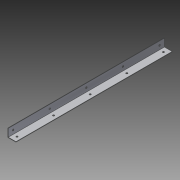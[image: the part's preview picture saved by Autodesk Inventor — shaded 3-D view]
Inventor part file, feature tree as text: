
AUTODESK INVENTOR PART (.ipt)
format: ipt  version: 2014 SP1 (Build 180222100, 222)  size: 107,520 bytes
history: native  units: in
note: dims shown in document units (in); Inventor stores cm internally (conversion verified against a paired STEP export)
features: extrude x3, sketch x3
ambient origin geometry x8: Origin, YZ Plane, XZ Plane, XY Plane, X Axis, Y Axis, Z Axis, Center Point
bodies: Solid1 (feature_tree)
feature tree (6):
  extrude  "Extrusion1"  Depth=0.0312in
  sketch  "Sketch2"  dims[d2=12.0in d3=0.0in d4=0.375in]
  sketch  "Sketch3"  dims[d5=0.125in d6=12.0in d7=1.9685in d9=2.8125in d10=0.3937in d12=1.0in d14=0.125in d15=0.375in d16=12.0in d17=1.9685in d19=2.8125in d20=0.3937in d22=1.0in d24=1.0in d25=0.0in d26=1.0in d27=0.0in]
  extrude  "Extrusion2"  Depth=12.0in
  extrude  "Extrusion3"  Depth=12.0in
  sketch  "Sketch1"  dims[d0=0.625in d1=0.0312in]
